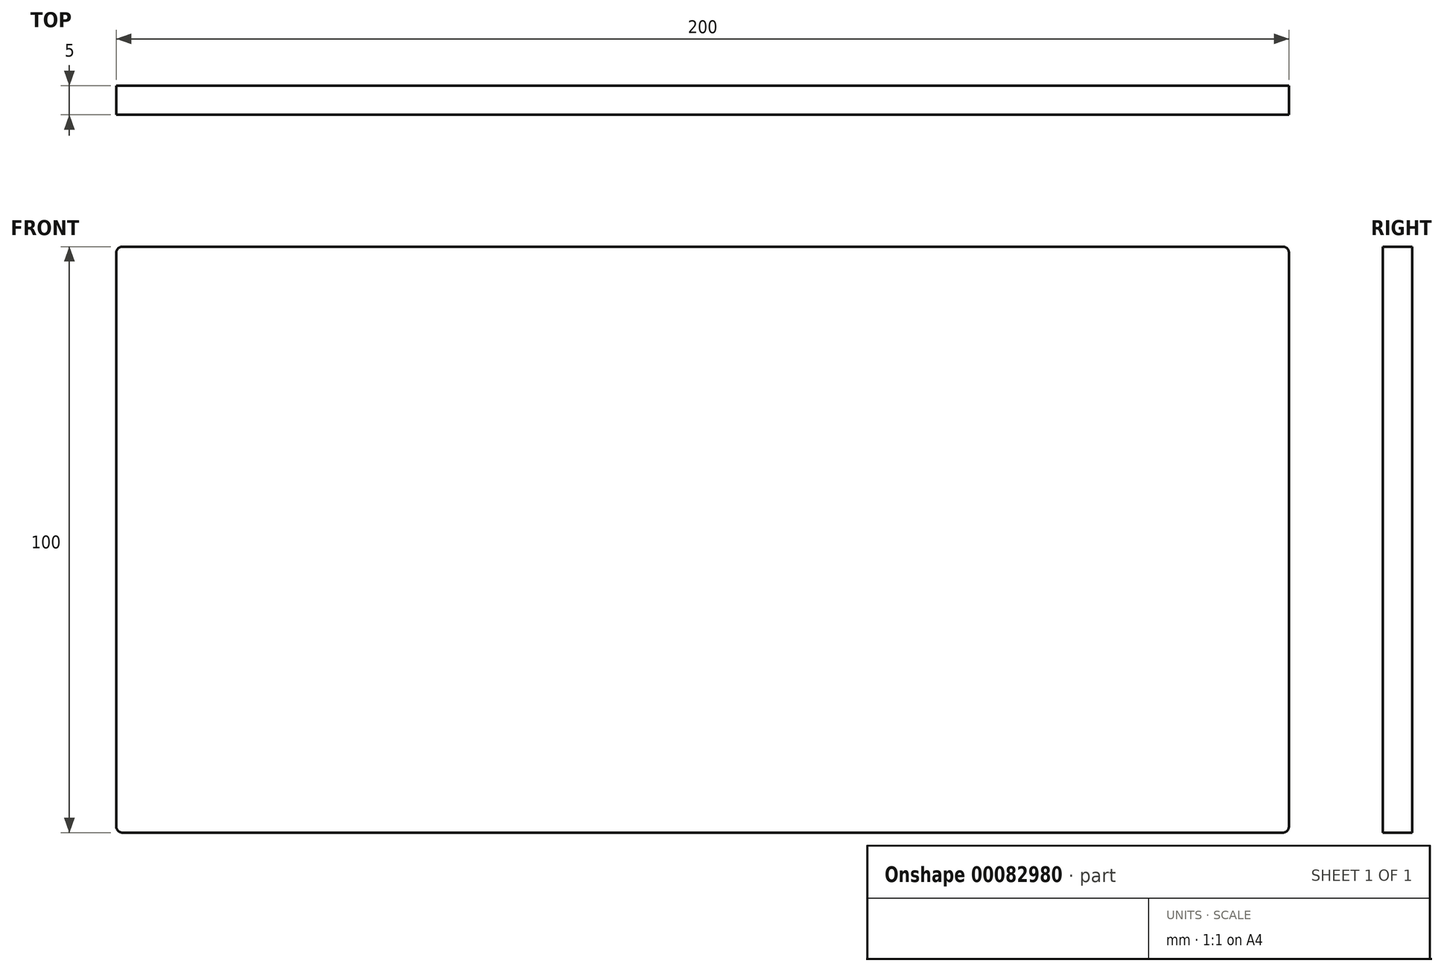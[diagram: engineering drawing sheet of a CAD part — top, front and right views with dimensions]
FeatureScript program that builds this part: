
annotation { "Feature Type Name" : "Feature", "Feature Type Description" : "" }
export const myFeature = defineFeature(function(context is Context, id is Id, definition is map)
    precondition{}
    {
        {
            var Q0;
            Q0=qCreatedBy(makeId("Front.planeOp"),FACE);
            var sketch = newSketch(context, id + "F0", { "sketchPlane" : qUnion([Q0])});
            skLineSegment(sketch, "E0.bottom", {"start": v(-97.72, 36.06) * mm, "end": v(102.28, 36.06) * mm});
            skLineSegment(sketch, "E0.top", {"start": v(-97.72, -63.94) * mm, "end": v(102.28, -63.94) * mm});
            skLineSegment(sketch, "E0.left", {"start": v(-97.72, 36.06) * mm, "end": v(-97.72, -63.94) * mm});
            skLineSegment(sketch, "E0.right", {"start": v(102.28, 36.06) * mm, "end": v(102.28, -63.94) * mm});
            skSolve(sketch);
        }
        {
            var Q0;
            Q0 = qSketchRegion(id + "F0", true);
            var Q1;
            Q1=makeQuery(id+"F0.imprint","IMPRINT",FACE,{"disambiguationData":[TD([[makeQuery(id+"F0.imprint","IMPRINT",EDGE,{"derivedFrom":sQuery(id+"F0.wireOp",EDGE,"E0.bottom")}),-1.0]])]});
            extrude(context, id + "F1", {"entities" : qUnion([Q0, Q1]), "depth" : 5 * mm});
        }
        {
            var Q0;
            Q0=makeQuery(id+"F1.opExtrude","SWEPT_EDGE",EDGE,{"disambiguationData":[OSD([sQuery(id+"F0.wireOp",EDGE,"E0.bottom"),sQuery(id+"F0.wireOp",EDGE,"E0.left")])]});
            var Q1;
            Q1=makeQuery(id+"F1.opExtrude","SWEPT_EDGE",EDGE,{"disambiguationData":[OSD([sQuery(id+"F0.wireOp",EDGE,"E0.top"),sQuery(id+"F0.wireOp",EDGE,"E0.left")])]});
            var Q2;
            Q2=makeQuery(id+"F1.opExtrude","SWEPT_EDGE",EDGE,{"disambiguationData":[OSD([sQuery(id+"F0.wireOp",EDGE,"E0.top"),sQuery(id+"F0.wireOp",EDGE,"E0.right")])]});
            var Q3;
            Q3=makeQuery(id+"F1.opExtrude","SWEPT_EDGE",EDGE,{"disambiguationData":[OSD([sQuery(id+"F0.wireOp",EDGE,"E0.bottom"),sQuery(id+"F0.wireOp",EDGE,"E0.right")])]});
            fillet(context, id + "F2", {"entities" : qUnion([Q0, Q1, Q2, Q3]), "radius" : 1 * mm, "tangentPropagation" : true, "allowEdgeOverflow" : false});
        }
    });
